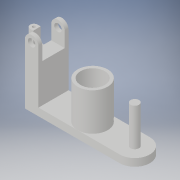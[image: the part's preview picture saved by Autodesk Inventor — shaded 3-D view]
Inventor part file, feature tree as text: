
AUTODESK INVENTOR PART (.ipt)
format: ipt  version: 2019 (Build 230136000, 136)  size: 194,048 bytes
history: native  units: in
note: dims shown in document units (in); Inventor stores cm internally (conversion verified against a paired STEP export)
features: extrude x7, sketch x7, fillet x1
ambient origin geometry x8: Origin, YZ Plane, XZ Plane, XY Plane, X Axis, Y Axis, Z Axis, Center Point
bodies: Solid1 (feature_tree)
feature tree (15):
  extrude  "Extrusion1"  Depth=0.1969in
  sketch  "Sketch2"  dims[d6=0.1772in d7=0.1969in]
  extrude  "Extrusion5"  Depth=0.1969in
  extrude  "Extrusion6"  Depth=0.3543in
  extrude  "Extrusion7"  Depth=0.7874in
  extrude  "Extrusion10"  Depth=0.7874in
  extrude  "Extrusion11"  Depth=0.3937in
  extrude  "Extrusion12"  Depth=0.3937in
  fillet  "Fillet4"  Radius=0.5984in
  sketch  "Sketch1"  dims[d0=1.5748in d2=0.1969in]
  sketch  "Sketch7"  dims[d8=0.3543in d9=2.126in]
  sketch  "Sketch9"  dims[d10=0.7874in d11=0.0in d12=0.1181in]
  sketch  "Sketch12"  dims[d13=0.2559in d14=0.7874in]
  sketch  "Sketch13"  dims[d16=1.0236in d19=0.3937in]
  sketch  "Sketch14"  dims[d20=0.2205in d21=0.3937in d22=0.5984in d40=0.5512in d41=0.5512in d42=0.5906in d43=0.5512in d44=0.0in d47=1.2795in d48=0.9843in d49=0.0in d50=0.6299in d51=1.2205in d52=0.0in d65=0.1969in d66=0.0in d67=0.0in d68=0.0787in d69=0.1969in d70=1.5748in d71=0.0in d72=0.1575in d73=0.3937in d74=0.7874in d75=0.0787in d76=1.1811in d77=0.0in d78=0.0787in]
